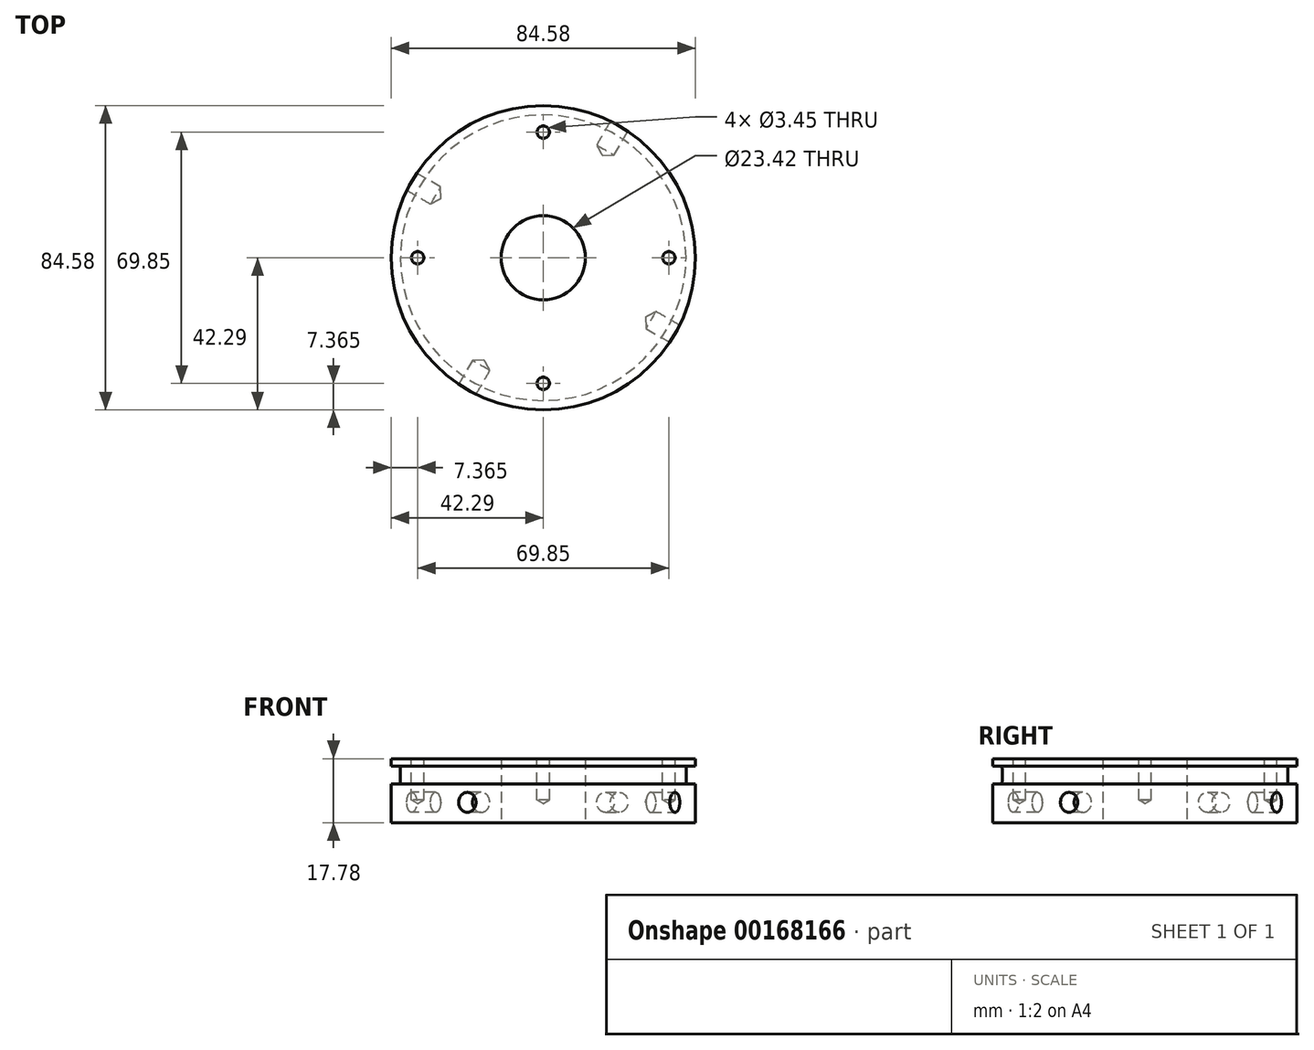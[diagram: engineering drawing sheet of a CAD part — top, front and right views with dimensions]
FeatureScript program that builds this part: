
annotation { "Feature Type Name" : "Feature", "Feature Type Description" : "" }
export const myFeature = defineFeature(function(context is Context, id is Id, definition is map)
    precondition{}
    {
        {
            var Q0;
            Q0=qCreatedBy(makeId("Top.planeOp"),FACE);
            var sketch = newSketch(context, id + "F0", { "sketchPlane" : qUnion([Q0])});
            skCircle(sketch, "E0", {"center": v(0, 0) * mm, "radius": 42.3 * mm});
            skSolve(sketch);
        }
        {
            var Q0;
            Q0=makeQuery(id+"F0.imprint","IMPRINT",FACE,{"disambiguationData":[TD([[makeQuery(id+"F0.imprint","IMPRINT",EDGE,{"derivedFrom":sQuery(id+"F0.wireOp",EDGE,"E0")}),1.0]])]});
            extrude(context, id + "F1", {"entities" : qUnion([Q0]), "depth" : 17.78 * mm});
        }
        {
            var Q0;
            {var subQ0=makeQuery(id+"FhJubWmbG7UBd7M_1.boolean.opBoolean","COPY",FACE,{"derivedFrom":makeQuery(id+"FhJubWmbG7UBd7M_1.opExtrude","SWEPT_FACE",FACE,{"disambiguationData":[OSD([sQuery(id+"FRuIeaWD6VeLny9_1.wireOp",EDGE,"idePJaX5-tPPE-BKw2-N1m4-zZUQrY6AHjir")])]})});Q0=makeQuery(id+"FOQC5dfjhO448EJ_1.boolean.opBoolean","SPLIT",FACE,{"disambiguationData":[TD([subQ0])],"derivedFrom":makeQuery(id+"FkcieFRIapZdHPD_1.boolean.opBoolean","SPLIT",FACE,{"disambiguationData":[TD([subQ0])],"derivedFrom":makeQuery(id+"F1.opExtrude","CAP_FACE",FACE,{"disambiguationData":[OSD([sQuery(id+"F0.wireOp",EDGE,"E0")])],"isStart":false})})});}
            var sketch = newSketch(context, id + "F2", { "sketchPlane" : qUnion([Q0])});
            skCircle(sketch, "E1", {"center": v(0, 0) * mm, "radius": 34.93 * mm, "construction": true});
            skLineSegment(sketch, "E2", {"start": v(0, 0) * mm, "end": v(34.93, 0) * mm, "construction": true});
            skPoint(sketch, "E3", {"position": v(34.93, 0) * mm});
            skPoint(sketch, "E4.1.0", {"position": v(0, 34.93) * mm});
            skPoint(sketch, "E4.2.0", {"position": v(-34.93, 0) * mm});
            skPoint(sketch, "E4.3.0", {"position": v(0, -34.93) * mm});
            skSolve(sketch);
        }
        {
            var Q0;
            Q0=sQuery(id+"F2.wireOp",VERTEX,"E3");
            var Q1;
            Q1=sQuery(id+"F2.wireOp",VERTEX,"E4.3.0");
            var Q2;
            Q2=sQuery(id+"F2.wireOp",VERTEX,"E4.2.0");
            var Q3;
            Q3=sQuery(id+"F2.wireOp",VERTEX,"E4.1.0");
            var Q4;
            Q4=makeQuery(id+"F1.opExtrude","SWEPT_BODY",BODY,{"disambiguationData":[OSD([sQuery(id+"F0.wireOp",EDGE,"E0")])]});
            hole(context, id + "F3", {"style" : HoleStyle.SIMPLE, "endStyle" : HoleEndStyle.BLIND, "standardTappedOrClearance" : lookupTablePath({ "standard" : "ANSI", "engagement" : "75%", "pitch" : "32 tpi", "size" : "#8", "type" : "Tapped" }), "standardBlindInLast" : lookupTablePath({ "standard" : "ANSI", "engagement" : "75%", "pitch" : "32 tpi", "size" : "#8", "type" : "Tapped" }), "holeDiameter" : 3.45 * mm, "holeDepth" : 11.43 * mm, "locations" : qUnion([Q0, Q1, Q2, Q3]), "scope" : qUnion([Q4]), "majorDiameter" : 4.17 * mm});
        }
        {
            var Q0;
            Q0=makeQuery(id+"FOQC5dfjhO448EJ_1.boolean.opBoolean","SPLIT",FACE,{"disambiguationData":[TD([makeQuery(id+"FhJubWmbG7UBd7M_1.boolean.opBoolean","COPY",FACE,{"derivedFrom":makeQuery(id+"FhJubWmbG7UBd7M_1.opExtrude","SWEPT_FACE",FACE,{"disambiguationData":[OSD([sQuery(id+"FRuIeaWD6VeLny9_1.wireOp",EDGE,"idePJaX5-tPPE-BKw2-N1m4-zZUQrY6AHjir")])]})})])],"derivedFrom":makeQuery(id+"F1.opExtrude","CAP_FACE",FACE,{"disambiguationData":[OSD([sQuery(id+"F0.wireOp",EDGE,"E0")])],"isStart":false})});
            cPlane(context, id + "F4", {"entities" : qUnion([Q0]), "cplaneType" : CPlaneType.OFFSET, "offset" : 2.03 * mm, "oppositeDirection" : true, "width" : 152.4 * mm, "height" : 152.4 * mm});
        }
        {
            var Q0;
            Q0=qCreatedBy(id+"F4.planeOp",FACE);
            var sketch = newSketch(context, id + "F5", { "sketchPlane" : qUnion([Q0])});
            skCircle(sketch, "E5", {"center": v(0, 0) * mm, "radius": 39.7 * mm});
            skCircle(sketch, "E6.0", {"center": v(0, 0) * mm, "radius": 42.3 * mm});
            skSolve(sketch);
        }
        {
            var Q0;
            Q0=qSketchRegion(id+"F5",true);
            extrude(context, id + "F6", {"entities" : qUnion([Q0]), "operationType" : NewBodyOperationType.REMOVE, "oppositeDirection" : true, "depth" : 5 * mm});
        }
        {
            var Q0;
            Q0=makeQuery(id+"F6.boolean.opBoolean","COPY",EDGE,{"derivedFrom":makeQuery(id+"F6.opExtrude","CAP_EDGE",EDGE,{"disambiguationData":[OSD([sQuery(id+"F5.wireOp",EDGE,"E5")])],"isStart":false})});
            var Q1;
            Q1=makeQuery(id+"F6.boolean.opBoolean","COPY",EDGE,{"derivedFrom":makeQuery(id+"F6.opExtrude","CAP_EDGE",EDGE,{"disambiguationData":[OSD([sQuery(id+"F5.wireOp",EDGE,"E5")])],"isStart":true})});
            fillet(context, id + "F7", {"entities" : qUnion([Q0, Q1]), "radius" : 0.76 * mm, "tangentPropagation" : true, "allowEdgeOverflow" : false});
        }
        {
            var Q0;
            {var subQ1=sQuery(id+"F0.wireOp",EDGE,"E0");var subQ2=makeQuery(id+"F1.opExtrude","SWEPT_FACE",FACE,{"disambiguationData":[OSD([subQ1])]});Q0=makeQuery(id+"FkcieFRIapZdHPD_1.boolean.opBoolean","SPLIT",FACE,{"disambiguationData":[TD([subQ2])],"derivedFrom":makeQuery(id+"F1.opExtrude","CAP_FACE",FACE,{"disambiguationData":[OSD([subQ1])],"isStart":false})});}
            var sketch = newSketch(context, id + "F8", { "sketchPlane" : qUnion([Q0])});
            skCircle(sketch, "E7.0", {"center": v(0, 0) * mm, "radius": 42.3 * mm, "construction": true});
            skPoint(sketch, "E8", {"position": v(-21.15, -36.63) * mm});
            skLineSegment(sketch, "E9", {"start": v(0, -42.3) * mm, "end": v(0, 0) * mm, "construction": true});
            skLineSegment(sketch, "E10", {"start": v(0, 0) * mm, "end": v(-17.96, -31.1) * mm, "construction": true});
            skLineSegment(sketch, "E11", {"start": v(-17.96, -31.1) * mm, "end": v(-21.15, -36.63) * mm, "construction": true});
            skLineSegment(sketch, "E12", {"start": v(0, 0) * mm, "end": v(21.15, 36.63) * mm, "construction": true});
            skLineSegment(sketch, "E13", {"start": v(21.15, 36.63) * mm, "end": v(0, 0) * mm, "construction": true});
            skLineSegment(sketch, "E14", {"start": v(36.63, -21.15) * mm, "end": v(0, 0) * mm, "construction": true});
            skLineSegment(sketch, "E15", {"start": v(0, 0) * mm, "end": v(-36.63, 21.15) * mm, "construction": true});
            skPoint(sketch, "E16", {"position": v(21.15, 36.63) * mm});
            skPoint(sketch, "E17", {"position": v(36.63, -21.15) * mm});
            skPoint(sketch, "E18", {"position": v(-36.63, 21.15) * mm});
            skSolve(sketch);
        }
        {
            var Q0;
            Q0=qCreatedBy(makeId("Front.planeOp"),FACE);
            var sketch = newSketch(context, id + "F9", { "sketchPlane" : qUnion([Q0])});
            skLineSegment(sketch, "E19", {"start": v(0, 0) * mm, "end": v(0, 38.57) * mm, "construction": true});
            skSolve(sketch);
        }
        {
            var Q0;
            Q0=sQuery(id+"F9.wireOp",EDGE,"E19");
            cPlane(context, id + "F10", {"entities" : qUnion([Q0]), "cplaneType" : CPlaneType.LINE_ANGLE, "offset" : 25.4 * mm, "angle" : 60 * degree, "width" : 152.4 * mm, "height" : 152.4 * mm});
        }
        {
            var Q0;
            Q0=sQuery(id+"F8.wireOp",VERTEX,"E8");
            var Q1;
            Q1=qCreatedBy(id+"F10.planeOp",FACE);
            cPlane(context, id + "F11", {"entities" : qUnion([Q0, Q1]), "cplaneType" : CPlaneType.PLANE_POINT, "offset" : 25.4 * mm, "width" : 152.4 * mm, "height" : 152.4 * mm});
        }
        {
            var Q0;
            Q0=qCreatedBy(id+"F11.planeOp",FACE);
            var Q1;
            Q1=sQuery(id+"F8.wireOp",VERTEX,"E16");
            cPlane(context, id + "F12", {"entities" : qUnion([Q0, Q1]), "cplaneType" : CPlaneType.PLANE_POINT, "offset" : 25.4 * mm, "width" : 152.4 * mm, "height" : 152.4 * mm});
        }
        {
            var Q0;
            Q0=sQuery(id+"F9.wireOp",EDGE,"E19");
            cPlane(context, id + "F13", {"entities" : qUnion([Q0]), "cplaneType" : CPlaneType.LINE_ANGLE, "offset" : 25.4 * mm, "angle" : 150 * degree, "width" : 152.4 * mm, "height" : 152.4 * mm});
        }
        {
            var Q0;
            Q0=sQuery(id+"F8.wireOp",VERTEX,"E18");
            var Q1;
            Q1=qCreatedBy(id+"F13.planeOp",FACE);
            cPlane(context, id + "F14", {"entities" : qUnion([Q0, Q1]), "cplaneType" : CPlaneType.PLANE_POINT, "offset" : 25.4 * mm, "width" : 152.4 * mm, "height" : 152.4 * mm});
        }
        {
            var Q0;
            Q0=qCreatedBy(id+"F13.planeOp",FACE);
            var Q1;
            Q1=sQuery(id+"F8.wireOp",VERTEX,"E17");
            cPlane(context, id + "F15", {"entities" : qUnion([Q0, Q1]), "cplaneType" : CPlaneType.PLANE_POINT, "offset" : 25.4 * mm, "width" : 152.4 * mm, "height" : 152.4 * mm});
        }
        {
            var Q0;
            Q0=qCreatedBy(id+"F11.planeOp",FACE);
            var sketch = newSketch(context, id + "F16", { "sketchPlane" : qUnion([Q0])});
            skLineSegment(sketch, "E20", {"start": v(0, 0) * mm, "end": v(0, 5.66) * mm, "construction": true});
            skPoint(sketch, "E21", {"position": v(0, 5.66) * mm});
            skSolve(sketch);
        }
        {
            var Q0;
            Q0=qCreatedBy(id+"F12.planeOp",FACE);
            var sketch = newSketch(context, id + "F17", { "sketchPlane" : qUnion([Q0])});
            skPoint(sketch, "E22", {"position": v(0, 5.66) * mm});
            skLineSegment(sketch, "E23.0", {"start": v(0, 0) * mm, "end": v(0, 5.66) * mm, "construction": true});
            skSolve(sketch);
        }
        {
            var Q0;
            Q0=qCreatedBy(id+"F14.planeOp",FACE);
            var sketch = newSketch(context, id + "F18", { "sketchPlane" : qUnion([Q0])});
            skLineSegment(sketch, "E24", {"start": v(0, 0) * mm, "end": v(0, 5.66) * mm, "construction": true});
            skLineSegment(sketch, "E25.0", {"start": v(-42.3, 0) * mm, "end": v(-42.3, 5.66) * mm, "construction": true});
            skPoint(sketch, "E26", {"position": v(0, 5.66) * mm});
            skLineSegment(sketch, "E27", {"start": v(-42.3, 5.66) * mm, "end": v(0, 5.66) * mm, "construction": true});
            skSolve(sketch);
        }
        {
            var Q0;
            Q0=qCreatedBy(id+"F15.planeOp",FACE);
            var sketch = newSketch(context, id + "F19", { "sketchPlane" : qUnion([Q0])});
            skLineSegment(sketch, "E28.0", {"start": v(0, 0) * mm, "end": v(0, 5.66) * mm, "construction": true});
            skPoint(sketch, "E29", {"position": v(0, 5.66) * mm});
            skSolve(sketch);
        }
        {
            var Q0;
            Q0=sQuery(id+"F19.wireOp",VERTEX,"E29");
            var Q1;
            Q1=makeQuery(id+"F1.opExtrude","SWEPT_BODY",BODY,{"disambiguationData":[OSD([sQuery(id+"F0.wireOp",EDGE,"E0")])]});
            hole(context, id + "F20", {"style" : HoleStyle.SIMPLE, "endStyle" : HoleEndStyle.BLIND, "oppositeDirection" : true, "standardTappedOrClearance" : lookupTablePath({ "standard" : "ANSI", "engagement" : "75%", "pitch" : "32 tpi", "size" : "1/4", "type" : "Tapped" }), "standardBlindInLast" : lookupTablePath({ "standard" : "ANSI", "engagement" : "75%", "pitch" : "32 tpi", "size" : "1/4", "type" : "Tapped" }), "holeDiameter" : 5.56 * mm, "holeDepth" : 7.62 * mm, "locations" : qUnion([Q0]), "scope" : qUnion([Q1]), "majorDiameter" : 6.35 * mm});
        }
        {
            var Q0;
            Q0=sQuery(id+"F18.wireOp",VERTEX,"E26");
            var Q1;
            Q1=makeQuery(id+"F1.opExtrude","SWEPT_BODY",BODY,{"disambiguationData":[OSD([sQuery(id+"F0.wireOp",EDGE,"E0")])]});
            hole(context, id + "F21", {"style" : HoleStyle.SIMPLE, "endStyle" : HoleEndStyle.BLIND, "standardTappedOrClearance" : lookupTablePath({ "standard" : "ANSI", "engagement" : "75%", "pitch" : "32 tpi", "size" : "1/4", "type" : "Tapped" }), "standardBlindInLast" : lookupTablePath({ "standard" : "ANSI", "engagement" : "75%", "pitch" : "32 tpi", "size" : "1/4", "type" : "Tapped" }), "holeDiameter" : 5.56 * mm, "holeDepth" : 7.62 * mm, "locations" : qUnion([Q0]), "scope" : qUnion([Q1]), "majorDiameter" : 6.35 * mm});
        }
        {
            var Q0;
            Q0=sQuery(id+"F16.wireOp",VERTEX,"E21");
            var Q1;
            Q1=makeQuery(id+"F1.opExtrude","SWEPT_BODY",BODY,{"disambiguationData":[OSD([sQuery(id+"F0.wireOp",EDGE,"E0")])]});
            hole(context, id + "F22", {"style" : HoleStyle.SIMPLE, "endStyle" : HoleEndStyle.BLIND, "oppositeDirection" : true, "standardTappedOrClearance" : lookupTablePath({ "standard" : "ANSI", "engagement" : "75%", "pitch" : "32 tpi", "size" : "1/4", "type" : "Tapped" }), "standardBlindInLast" : lookupTablePath({ "standard" : "ANSI", "engagement" : "75%", "pitch" : "32 tpi", "size" : "1/4", "type" : "Tapped" }), "holeDiameter" : 5.56 * mm, "holeDepth" : 7.62 * mm, "locations" : qUnion([Q0]), "scope" : qUnion([Q1]), "majorDiameter" : 6.35 * mm});
        }
        {
            var Q0;
            Q0=sQuery(id+"F17.wireOp",VERTEX,"E22");
            var Q1;
            Q1=makeQuery(id+"F1.opExtrude","SWEPT_BODY",BODY,{"disambiguationData":[OSD([sQuery(id+"F0.wireOp",EDGE,"E0")])]});
            hole(context, id + "F23", {"style" : HoleStyle.SIMPLE, "endStyle" : HoleEndStyle.BLIND, "standardTappedOrClearance" : lookupTablePath({ "standard" : "ANSI", "engagement" : "75%", "pitch" : "32 tpi", "size" : "1/4", "type" : "Tapped" }), "standardBlindInLast" : lookupTablePath({ "standard" : "ANSI", "engagement" : "75%", "pitch" : "32 tpi", "size" : "1/4", "type" : "Tapped" }), "holeDiameter" : 5.56 * mm, "holeDepth" : 7.62 * mm, "locations" : qUnion([Q0]), "scope" : qUnion([Q1]), "majorDiameter" : 6.35 * mm});
        }
        {
            var Q0;
            Q0=makeQuery(id+"F1.opExtrude","CAP_FACE",FACE,{"disambiguationData":[OSD([sQuery(id+"F0.wireOp",EDGE,"E0")])],"isStart":true});
            var sketch = newSketch(context, id + "F24", { "sketchPlane" : qUnion([Q0])});
            skPoint(sketch, "E30", {"position": v(0, 0) * mm});
            skSolve(sketch);
        }
        {
            var Q0;
            Q0=sQuery(id+"F24.wireOp",VERTEX,"E30");
            var Q1;
            Q1=makeQuery(id+"F1.opExtrude","SWEPT_BODY",BODY,{"disambiguationData":[OSD([sQuery(id+"F0.wireOp",EDGE,"E0")])]});
            hole(context, id + "F25", {"style" : HoleStyle.SIMPLE, "endStyle" : HoleEndStyle.THROUGH, "holeDiameter" : 23.42 * mm, "locations" : qUnion([Q0]), "scope" : qUnion([Q1]), "isTappedThrough" : true});
        }
    });
